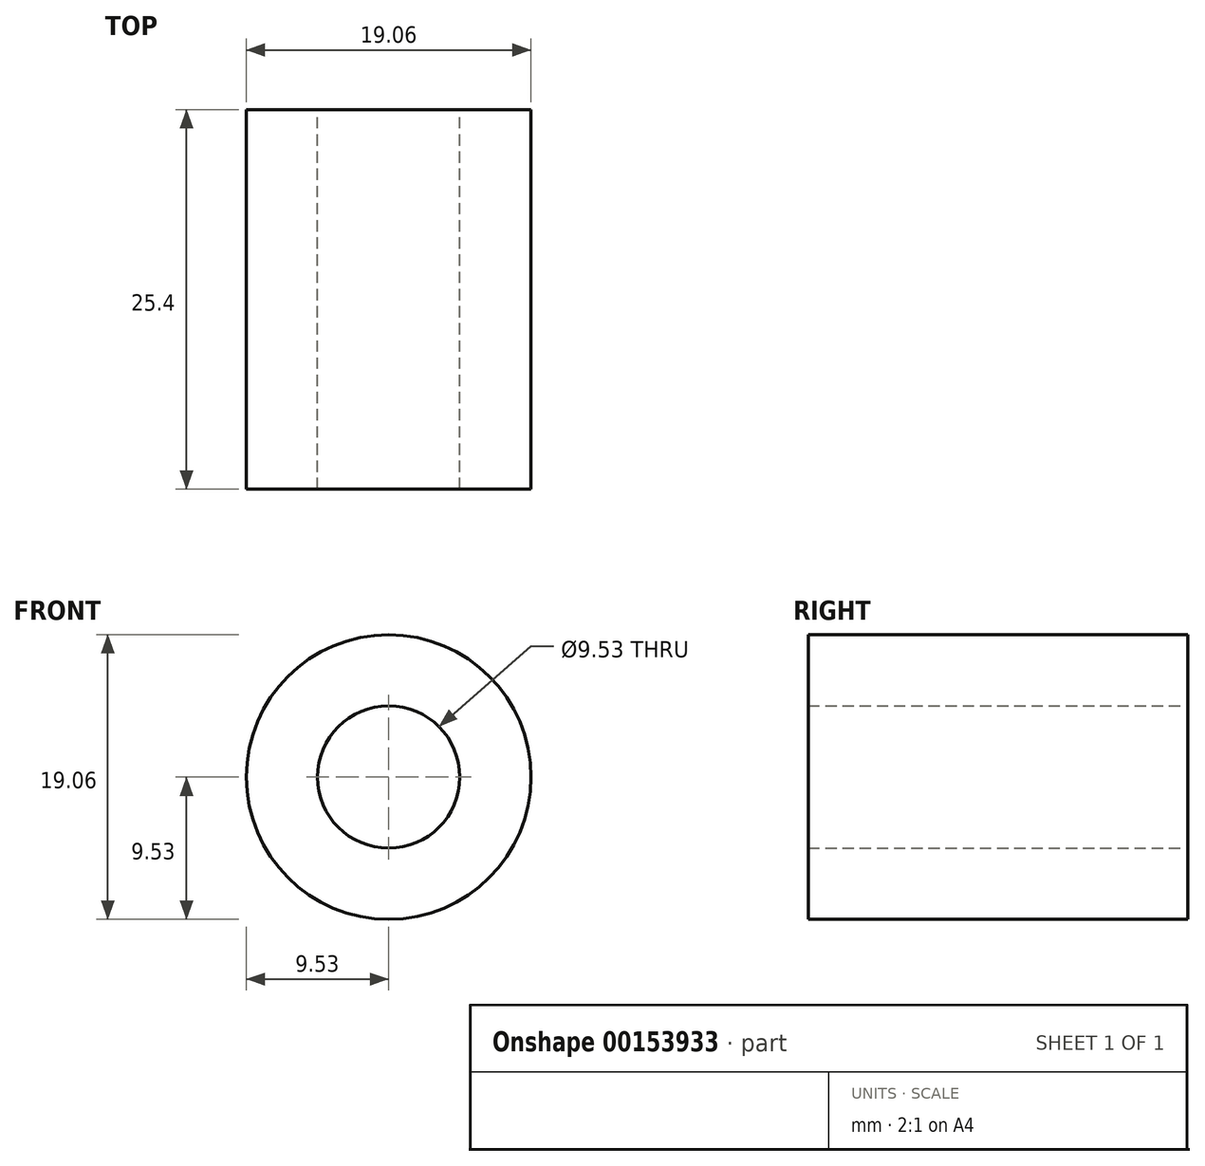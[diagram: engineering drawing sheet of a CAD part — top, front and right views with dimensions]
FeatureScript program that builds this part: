
annotation { "Feature Type Name" : "Feature", "Feature Type Description" : "" }
export const myFeature = defineFeature(function(context is Context, id is Id, definition is map)
    precondition{}
    {
        {
            var Q0;
            Q0=qCreatedBy(makeId("Front.planeOp"),FACE);
            var sketch = newSketch(context, id + "F0", { "sketchPlane" : qUnion([Q0])});
            skCircle(sketch, "E0", {"center": v(0, 0) * mm, "radius": 9.53 * mm});
            skSolve(sketch);
        }
        {
            var Q0;
            Q0 = qSketchRegion(id + "F0", true);
            extrude(context, id + "F1", {"entities" : qUnion([Q0]), "depth" : 25.4 * mm});
        }
        {
            var Q0;
            Q0=qCreatedBy(makeId("Front.planeOp"),FACE);
            var sketch = newSketch(context, id + "F2", { "sketchPlane" : qUnion([Q0])});
            skLineSegment(sketch, "E1.bottom", {"start": v(4.76, 4.76) * mm, "end": v(-4.76, 4.76) * mm});
            skLineSegment(sketch, "E1.top", {"start": v(4.76, -4.76) * mm, "end": v(-4.76, -4.76) * mm});
            skLineSegment(sketch, "E1.left", {"start": v(4.76, 4.76) * mm, "end": v(4.76, -4.76) * mm});
            skLineSegment(sketch, "E1.right", {"start": v(-4.76, 4.76) * mm, "end": v(-4.76, -4.76) * mm});
            skPoint(sketch, "E1.middle", {"position": v(0, 0) * mm});
            skCircle(sketch, "E2", {"center": v(0, 0) * mm, "radius": 4.76 * mm});
            skSolve(sketch);
        }
        {
            var Q0;
            Q0=sQuery(id+"F2.wireOp",VERTEX,"E1.middle");
            var Q1;
            Q1=makeQuery(id+"F1.opExtrude","SWEPT_BODY",BODY,{"disambiguationData":[OSD([sQuery(id+"F0.wireOp",EDGE,"E0")])]});
            hole(context, id + "F3", {"style" : HoleStyle.SIMPLE, "endStyle" : HoleEndStyle.THROUGH, "oppositeDirection" : true, "holeDiameter" : 9.52 * mm, "locations" : qUnion([Q0]), "scope" : qUnion([Q1]), "isTappedThrough" : true});
        }
        {
            var Q0;
            Q0=qCreatedBy(makeId("Front.planeOp"),FACE);
            var sketch = newSketch(context, id + "F4", { "sketchPlane" : qUnion([Q0])});
            skLineSegment(sketch, "E3.bottom", {"start": v(-4.76, 4.51) * mm, "end": v(4.76, 4.51) * mm});
            skLineSegment(sketch, "E3.top", {"start": v(-4.76, -4.51) * mm, "end": v(4.76, -4.51) * mm});
            skLineSegment(sketch, "E3.left", {"start": v(-4.76, 4.51) * mm, "end": v(-4.76, -4.51) * mm});
            skLineSegment(sketch, "E3.right", {"start": v(4.76, 4.51) * mm, "end": v(4.76, -4.51) * mm});
            skPoint(sketch, "E3.middle", {"position": v(0, 0) * mm});
            skSolve(sketch);
        }
        {
            var Q0;
            Q0=sQuery(id+"F4.wireOp",EDGE,"E3.bottom");
            var Q1;
            Q1=sQuery(id+"F4.wireOp",EDGE,"E3.right");
            var Q2;
            Q2=sQuery(id+"F4.wireOp",EDGE,"E3.left");
            var Q3;
            Q3=sQuery(id+"F4.wireOp",EDGE,"E3.top");
            extrude(context, id + "F5", {"bodyType" : ToolBodyType.SURFACE, "surfaceEntities" : qUnion([Q0, Q1, Q2, Q3]), "depth" : 10.16 * mm});
        }
    });
